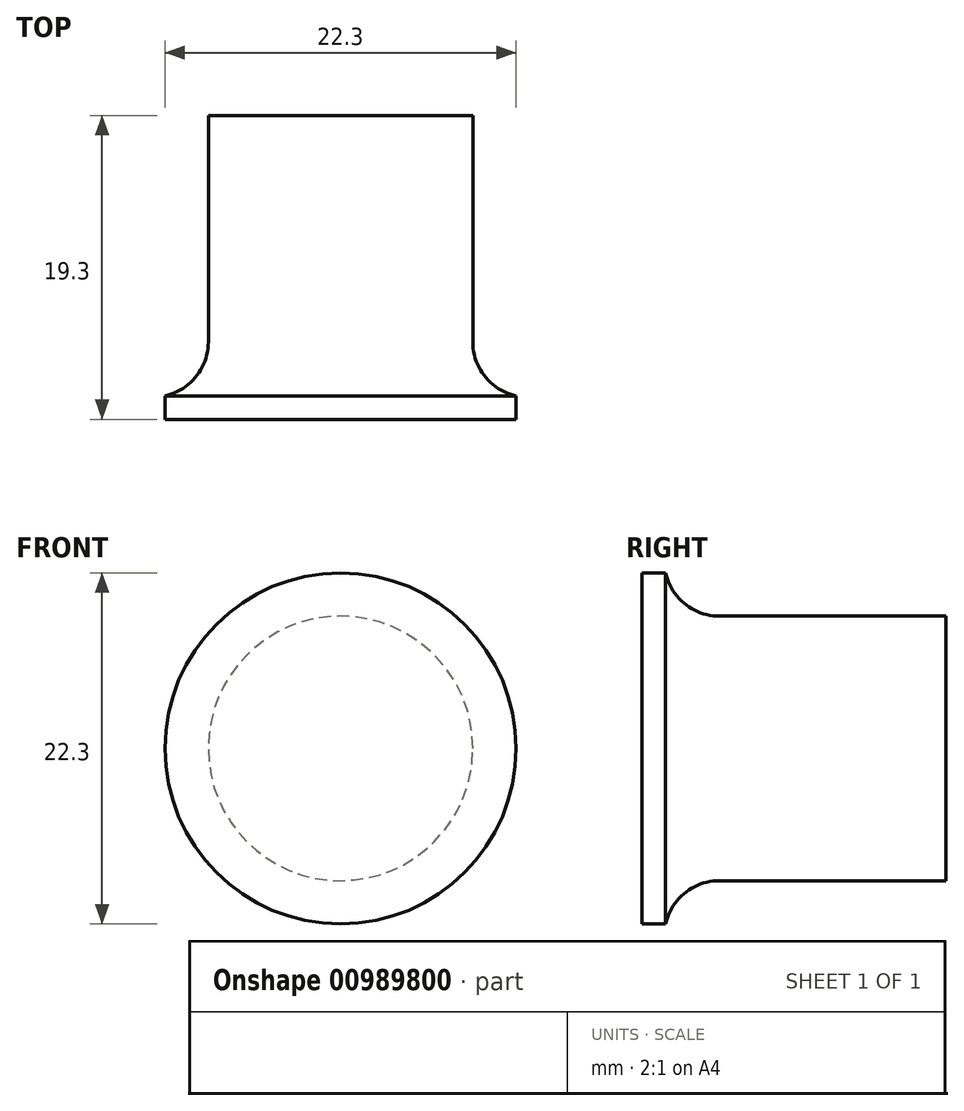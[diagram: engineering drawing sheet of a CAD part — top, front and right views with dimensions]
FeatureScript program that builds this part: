
annotation { "Feature Type Name" : "Feature", "Feature Type Description" : "" }
export const myFeature = defineFeature(function(context is Context, id is Id, definition is map)
    precondition{}
    {
        {
            var Q0;
            Q0=qCreatedBy(makeId("Front.planeOp"),FACE);
            var sketch = newSketch(context, id + "F0", { "sketchPlane" : qUnion([Q0])});
            skCircle(sketch, "E0", {"center": v(0, 0) * mm, "radius": 11.15 * mm});
            skSolve(sketch);
        }
        {
            var Q0;
            Q0 = qSketchRegion(id + "F0", true);
            extrude(context, id + "F1", {"entities" : qUnion([Q0]), "depth" : 19.3 * mm, "offsetDistance" : 25 * mm});
        }
        {
            var Q0;
            Q0=makeQuery(id+"F1.opExtrude","CAP_FACE",FACE,{"disambiguationData":[OSD([sQuery(id+"F0.wireOp",EDGE,"E0")])],"isStart":false});
            var sketch = newSketch(context, id + "F2", { "sketchPlane" : qUnion([Q0])});
            skCircle(sketch, "E1", {"center": v(0, 0) * mm, "radius": 8.4 * mm});
            skCircle(sketch, "E2", {"center": v(0, 0) * mm, "radius": 11.15 * mm});
            skSolve(sketch);
        }
        {
            var Q0;
            Q0 = qSketchRegion(id + "F2", true);
            var Q1;
            Q1=makeQuery(id+"F1.opExtrude","CAP_FACE",FACE,{"disambiguationData":[OSD([sQuery(id+"F0.wireOp",EDGE,"E0")])],"isStart":true});
            extrude(context, id + "F3", {"entities" : qUnion([Q0]), "operationType" : NewBodyOperationType.REMOVE, "endBound" : BoundingType.UP_TO_SURFACE, "oppositeDirection" : true, "depth" : 25 * mm, "endBoundEntityFace" : qUnion([Q1]), "offsetDistance" : 25 * mm, "hasSecondDirection" : true, "secondDirectionOppositeDirection" : true, "secondDirectionDepth" : 1.5 * mm});
        }
        {
            var Q0;
            Q0=makeQuery(id+"F3.boolean.opBoolean","COPY",EDGE,{"derivedFrom":makeQuery(id+"F3.opExtrude","CAP_EDGE",EDGE,{"disambiguationData":[OSD([sQuery(id+"F2.wireOp",EDGE,"E1")])],"isStart":true})});
            fillet(context, id + "F4", {"entities" : qUnion([Q0]), "radius" : 3.5 * mm, "tangentPropagation" : true, "allowEdgeOverflow" : false});
        }
    });
